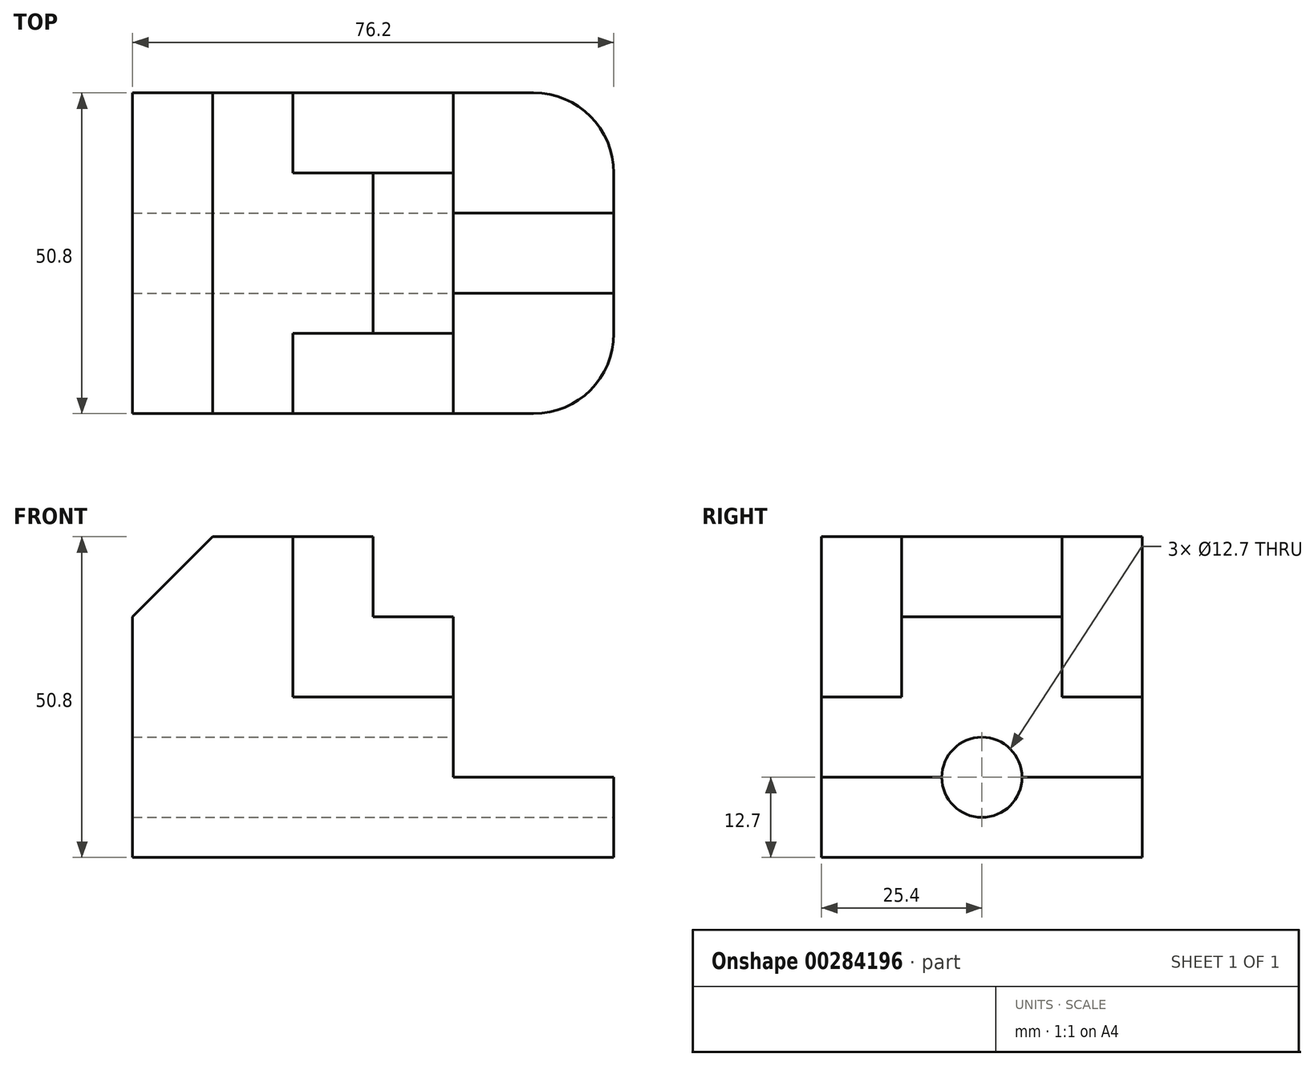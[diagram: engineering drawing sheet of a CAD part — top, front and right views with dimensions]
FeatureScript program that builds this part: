
annotation { "Feature Type Name" : "Feature", "Feature Type Description" : "" }
export const myFeature = defineFeature(function(context is Context, id is Id, definition is map)
    precondition{}
    {
        {
            var Q0;
            Q0=qCreatedBy(makeId("Front.planeOp"),FACE);
            var sketch = newSketch(context, id + "F0", { "sketchPlane" : qUnion([Q0])});
            skLineSegment(sketch, "E0", {"start": v(0, 0) * mm, "end": v(76.2, 0) * mm});
            skLineSegment(sketch, "E1", {"start": v(76.2, 0) * mm, "end": v(76.2, 12.7) * mm});
            skLineSegment(sketch, "E2", {"start": v(76.2, 12.7) * mm, "end": v(50.8, 12.7) * mm});
            skLineSegment(sketch, "E3", {"start": v(50.8, 12.7) * mm, "end": v(50.8, 38.1) * mm});
            skLineSegment(sketch, "E4", {"start": v(50.8, 38.1) * mm, "end": v(38.1, 38.1) * mm});
            skLineSegment(sketch, "E5", {"start": v(38.1, 38.1) * mm, "end": v(38.1, 50.8) * mm});
            skLineSegment(sketch, "E6", {"start": v(38.1, 50.8) * mm, "end": v(12.7, 50.8) * mm});
            skLineSegment(sketch, "E7", {"start": v(12.7, 50.8) * mm, "end": v(0, 38.1) * mm});
            skLineSegment(sketch, "E8", {"start": v(0, 38.1) * mm, "end": v(0, 0) * mm});
            skSolve(sketch);
        }
        {
            var Q0;
            Q0=makeQuery(id+"F0.imprint","IMPRINT",FACE,{"disambiguationData":[TD([[makeQuery(id+"F0.imprint","IMPRINT",EDGE,{"derivedFrom":sQuery(id+"F0.wireOp",EDGE,"E0")}),1.0]])]});
            extrude(context, id + "F1", {"entities" : qUnion([Q0]), "depth" : 50.8 * mm});
        }
        {
            var Q0;
            Q0=makeQuery(id+"F1.opExtrude","SWEPT_FACE",FACE,{"disambiguationData":[OSD([sQuery(id+"F0.wireOp",EDGE,"E3")])]});
            var sketch = newSketch(context, id + "F2", { "sketchPlane" : qUnion([Q0])});
            skLineSegment(sketch, "E9.bottom", {"start": v(-50.8, 25.4) * mm, "end": v(-38.1, 25.4) * mm});
            skLineSegment(sketch, "E9.top", {"start": v(-50.8, 50.8) * mm, "end": v(-38.1, 50.8) * mm});
            skLineSegment(sketch, "E9.left", {"start": v(-50.8, 25.4) * mm, "end": v(-50.8, 50.8) * mm});
            skLineSegment(sketch, "E9.right", {"start": v(-38.1, 25.4) * mm, "end": v(-38.1, 50.8) * mm});
            skLineSegment(sketch, "E10.bottom", {"start": v(0, 25.4) * mm, "end": v(-12.7, 25.4) * mm});
            skLineSegment(sketch, "E10.top", {"start": v(0, 50.8) * mm, "end": v(-12.7, 50.8) * mm});
            skLineSegment(sketch, "E10.left", {"start": v(0, 25.4) * mm, "end": v(0, 50.8) * mm});
            skLineSegment(sketch, "E10.right", {"start": v(-12.7, 25.4) * mm, "end": v(-12.7, 50.8) * mm});
            skSolve(sketch);
        }
        {
            var Q0;
            Q0 = qSketchRegion(id + "F2", true);
            extrude(context, id + "F3", {"entities" : qUnion([Q0]), "operationType" : NewBodyOperationType.REMOVE, "oppositeDirection" : true, "depth" : 25.4 * mm});
        }
        {
            var Q0;
            Q0=makeQuery(id+"F1.opExtrude","CAP_EDGE",EDGE,{"disambiguationData":[OSD([sQuery(id+"F0.wireOp",EDGE,"E1")])],"isStart":true});
            var Q1;
            Q1=makeQuery(id+"F1.opExtrude","CAP_EDGE",EDGE,{"disambiguationData":[OSD([sQuery(id+"F0.wireOp",EDGE,"E1")])],"isStart":false});
            fillet(context, id + "F4", {"entities" : qUnion([Q0, Q1]), "radius" : 12.7 * mm, "tangentPropagation" : true, "allowEdgeOverflow" : false});
        }
        {
            var Q0;
            Q0=makeQuery(id+"F1.opExtrude","SWEPT_FACE",FACE,{"disambiguationData":[OSD([sQuery(id+"F0.wireOp",EDGE,"E1")])]});
            var sketch = newSketch(context, id + "F5", { "sketchPlane" : qUnion([Q0])});
            skCircle(sketch, "E11", {"center": v(-25.4, 12.7) * mm, "radius": 6.35 * mm});
            skSolve(sketch);
        }
        {
            var Q0;
            Q0 = qSketchRegion(id + "F5", true);
            extrude(context, id + "F6", {"entities" : qUnion([Q0]), "operationType" : NewBodyOperationType.REMOVE, "oppositeDirection" : true, "depth" : 76.2 * mm});
        }
    });
